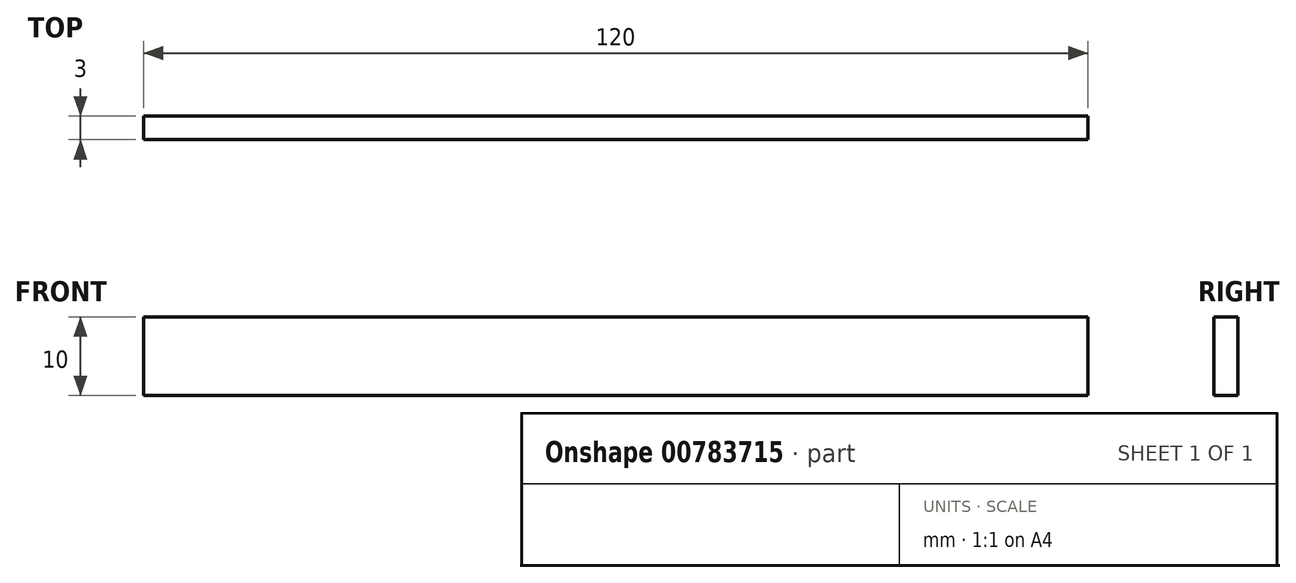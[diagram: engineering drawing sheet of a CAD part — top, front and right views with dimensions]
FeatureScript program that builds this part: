
annotation { "Feature Type Name" : "Feature", "Feature Type Description" : "" }
export const myFeature = defineFeature(function(context is Context, id is Id, definition is map)
    precondition{}
    {
        {
            var Q0;
            Q0=qCreatedBy(makeId("Front.planeOp"),FACE);
            var sketch = newSketch(context, id + "F0", { "sketchPlane" : qUnion([Q0])});
            skLineSegment(sketch, "E0.bottom", {"start": v(-120, 10) * mm, "end": v(0, 10) * mm});
            skLineSegment(sketch, "E0.top", {"start": v(-120, 0) * mm, "end": v(0, 0) * mm});
            skLineSegment(sketch, "E0.left", {"start": v(-120, 10) * mm, "end": v(-120, 0) * mm});
            skLineSegment(sketch, "E0.right", {"start": v(0, 10) * mm, "end": v(0, 0) * mm});
            skSolve(sketch);
        }
        {
            var Q0;
            Q0=makeQuery(id+"F0.imprint","IMPRINT",FACE,{"disambiguationData":[TD([[makeQuery(id+"F0.imprint","IMPRINT",EDGE,{"derivedFrom":sQuery(id+"F0.wireOp",EDGE,"E0.bottom")}),-1.0]])]});
            extrude(context, id + "F1", {"entities" : qUnion([Q0]), "depth" : 3 * mm, "offsetDistance" : 25 * mm});
        }
    });
